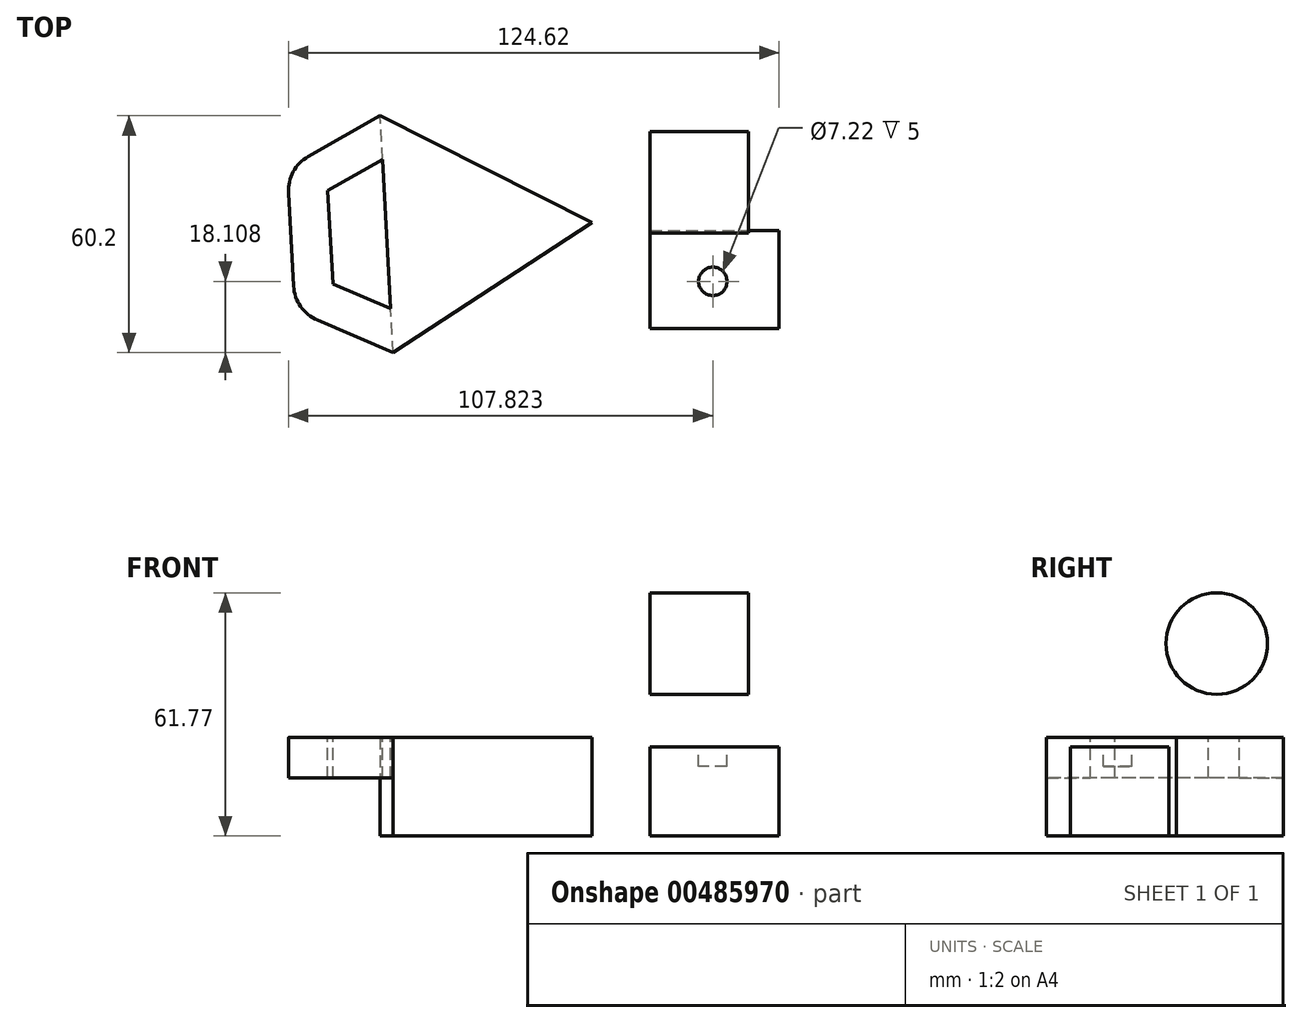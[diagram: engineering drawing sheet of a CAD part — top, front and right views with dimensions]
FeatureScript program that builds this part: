
annotation { "Feature Type Name" : "Feature", "Feature Type Description" : "" }
export const myFeature = defineFeature(function(context is Context, id is Id, definition is map)
    precondition{}
    {
        {
            var Q0;
            Q0=qCreatedBy(makeId("Front.planeOp"),FACE);
            var sketch = newSketch(context, id + "F0", { "sketchPlane" : qUnion([Q0])});
            skLineSegment(sketch, "E0.bottom", {"start": v(0, 22.61) * mm, "end": v(32.75, 22.61) * mm});
            skLineSegment(sketch, "E0.top", {"start": v(0, 0) * mm, "end": v(32.75, 0) * mm});
            skLineSegment(sketch, "E0.left", {"start": v(0, 22.61) * mm, "end": v(0, 0) * mm});
            skLineSegment(sketch, "E0.right", {"start": v(32.75, 22.61) * mm, "end": v(32.75, 0) * mm});
            skSolve(sketch);
        }
        {
            var Q0;
            Q0=makeQuery(id+"F0.imprint","IMPRINT",FACE,{"disambiguationData":[TD([[makeQuery(id+"F0.imprint","IMPRINT",EDGE,{"derivedFrom":sQuery(id+"F0.wireOp",EDGE,"E0.bottom")}),-1.0]])]});
            extrude(context, id + "F1", {"entities" : qUnion([Q0]), "depth" : 25 * mm});
        }
        {
            var Q0;
            Q0=qCreatedBy(makeId("Right.planeOp"),FACE);
            var sketch = newSketch(context, id + "F2", { "sketchPlane" : qUnion([Q0])});
            skCircle(sketch, "E1", {"center": v(12.22, 48.86) * mm, "radius": 12.9 * mm});
            skSolve(sketch);
        }
        {
            var Q0;
            Q0=makeQuery(id+"F2.imprint","IMPRINT",FACE,{"disambiguationData":[TD([[makeQuery(id+"F2.imprint","IMPRINT",EDGE,{"derivedFrom":sQuery(id+"F2.wireOp",EDGE,"E1")}),1.0]])]});
            extrude(context, id + "F3", {"entities" : qUnion([Q0]), "depth" : 25 * mm});
        }
        {
            var Q0;
            Q0=qCreatedBy(makeId("Top.planeOp"),FACE);
            var sketch = newSketch(context, id + "F4", { "sketchPlane" : qUnion([Q0])});
            skCircle(sketch, "E2.cCircle", {"center": v(-49.53, 0) * mm, "radius": 17.4 * mm, "construction": true});
            skLineSegment(sketch, "E2.0", {"start": v(-14.77, 1.92) * mm, "end": v(-65.25, -31.06) * mm});
            skLineSegment(sketch, "E2.1", {"start": v(-65.25, -31.06) * mm, "end": v(-68.58, 29.14) * mm});
            skLineSegment(sketch, "E2.2", {"start": v(-68.58, 29.14) * mm, "end": v(-14.77, 1.92) * mm});
            skPoint(sketch, "E2.0.midPoint", {"position": v(-40, -14.57) * mm});
            skSolve(sketch);
        }
        {
            var Q0;
            Q0=makeQuery(id+"F4.imprint","IMPRINT",FACE,{"disambiguationData":[TD([[makeQuery(id+"F4.imprint","IMPRINT",EDGE,{"derivedFrom":sQuery(id+"F4.wireOp",EDGE,"E2.0")}),-1.0]])]});
            extrude(context, id + "F5", {"entities" : qUnion([Q0]), "depth" : 25 * mm});
        }
        {
            var Q0;
            Q0=makeQuery(id+"F1.opExtrude","SWEPT_FACE",FACE,{"disambiguationData":[OSD([sQuery(id+"F0.wireOp",EDGE,"E0.bottom")])]});
            var sketch = newSketch(context, id + "F6", { "sketchPlane" : qUnion([Q0])});
            skCircle(sketch, "E3", {"center": v(15.95, -12.95) * mm, "radius": 3.61 * mm});
            skSolve(sketch);
        }
        {
            var Q0;
            Q0=makeQuery(id+"F6.imprint","IMPRINT",FACE,{"disambiguationData":[TD([[makeQuery(id+"F6.imprint","IMPRINT",EDGE,{"derivedFrom":sQuery(id+"F6.wireOp",EDGE,"E3")}),1.0]])]});
            extrude(context, id + "F7", {"entities" : qUnion([Q0]), "operationType" : NewBodyOperationType.REMOVE, "oppositeDirection" : true, "depth" : 5 * mm});
        }
        {
            var Q0;
            Q0=makeQuery(id+"F5.opExtrude","CAP_FACE",FACE,{"disambiguationData":[OSD([sQuery(id+"F4.wireOp",EDGE,"E2.0"),sQuery(id+"F4.wireOp",EDGE,"E2.1"),sQuery(id+"F4.wireOp",EDGE,"E2.2")])],"isStart":false});
            var sketch = newSketch(context, id + "F8", { "sketchPlane" : qUnion([Q0])});
            skLineSegment(sketch, "E4", {"start": v(-68.58, 29.14) * mm, "end": v(-86.8, 18.79) * mm});
            skLineSegment(sketch, "E5", {"start": v(-91.86, 9.54) * mm, "end": v(-90.54, -14.15) * mm});
            skLineSegment(sketch, "E6", {"start": v(-84.5, -22.79) * mm, "end": v(-65.25, -31.06) * mm});
            skLineSegment(sketch, "E7", {"start": v(-91.2, -2.3) * mm, "end": v(-66.91, -0.96) * mm, "construction": true});
            skPoint(sketch, "E8.visualSharp", {"position": v(-92.2, 15.73) * mm});
            skArc(sketch, "E8.filletArc", {"start": v(-86.8, 18.79) * mm, "mid": v(-90.65, 14.88) * mm, "end": v(-91.86, 9.54) * mm});
            skPoint(sketch, "E9.visualSharp", {"position": v(-90.2, -20.34) * mm});
            skArc(sketch, "E9.filletArc", {"start": v(-90.54, -14.15) * mm, "mid": v(-88.76, -19.33) * mm, "end": v(-84.5, -22.79) * mm});
            skLineSegment(sketch, "E10.0", {"start": v(-80.56, -13.6) * mm, "end": v(-65.86, -19.92) * mm});
            skLineSegment(sketch, "E10.1", {"start": v(-67.96, 18) * mm, "end": v(-81.87, 10.1) * mm});
            skLineSegment(sketch, "E10.2", {"start": v(-81.87, 10.1) * mm, "end": v(-81.87, 10.1) * mm});
            skLineSegment(sketch, "E10.3", {"start": v(-81.87, 10.1) * mm, "end": v(-80.56, -13.6) * mm});
            skLineSegment(sketch, "E10.4", {"start": v(-80.56, -13.6) * mm, "end": v(-80.56, -13.6) * mm});
            skLineSegment(sketch, "E11.0.0", {"start": v(0, -0.69) * mm, "end": v(0, 25.12) * mm});
            skCircle(sketch, "E12.0", {"center": v(15.95, -12.95) * mm, "radius": 3.61 * mm});
            skLineSegment(sketch, "E13.0", {"start": v(0, -25) * mm, "end": v(32.75, -25) * mm});
            skLineSegment(sketch, "E14.0.0", {"start": v(25, 25.12) * mm, "end": v(25, -0.69) * mm});
            skLineSegment(sketch, "E15.0", {"start": v(-65.25, -31.06) * mm, "end": v(-68.58, 29.14) * mm});
            skSolve(sketch);
        }
        {
            var Q0;
            Q0=makeQuery(id+"F8.imprint","IMPRINT",FACE,{"disambiguationData":[TD([[makeQuery(id+"F8.imprint","IMPRINT",EDGE,{"derivedFrom":sQuery(id+"F8.wireOp",EDGE,"E4")}),1.0]])]});
            extrude(context, id + "F9", {"entities" : qUnion([Q0]), "operationType" : NewBodyOperationType.ADD, "oppositeDirection" : true, "depth" : 10.3 * mm, "offsetDistance" : 25 * mm});
        }
    });
